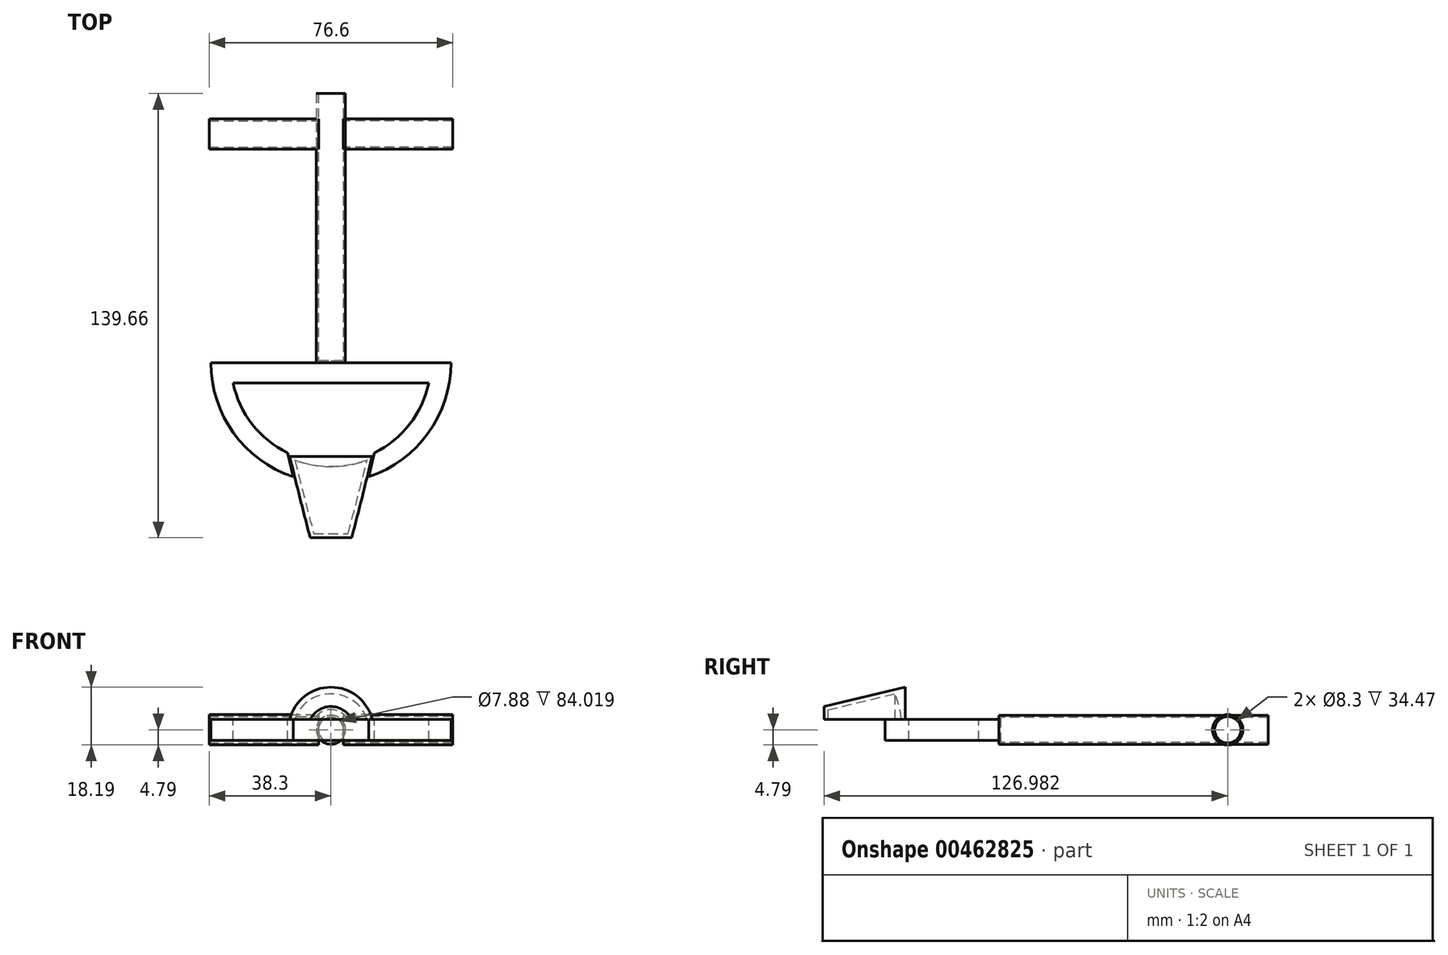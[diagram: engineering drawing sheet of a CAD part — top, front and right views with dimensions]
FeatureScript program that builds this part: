
annotation { "Feature Type Name" : "Feature", "Feature Type Description" : "" }
export const myFeature = defineFeature(function(context is Context, id is Id, definition is map)
    precondition{}
    {
        {
            var Q0;
            Q0=qCreatedBy(makeId("Top.planeOp"),FACE);
            var sketch = newSketch(context, id + "F0", { "sketchPlane" : qUnion([Q0])});
            skLineSegment(sketch, "E0.bottom", {"start": v(0, 0) * mm, "end": v(4.57, 0) * mm});
            skLineSegment(sketch, "E0.top", {"start": v(0, 84.65) * mm, "end": v(4.57, 84.65) * mm});
            skLineSegment(sketch, "E0.left", {"start": v(0, 0) * mm, "end": v(0, 84.65) * mm});
            skLineSegment(sketch, "E0.right", {"start": v(4.57, 0) * mm, "end": v(4.57, 84.65) * mm});
            skArc(sketch, "E1", {"start": v(-37.76, 0) * mm, "mid": v(0, -37.76) * mm, "end": v(37.76, 0) * mm});
            skLineSegment(sketch, "E2", {"start": v(-37.76, 0) * mm, "end": v(0, 0) * mm});
            skLineSegment(sketch, "E3", {"start": v(37.76, 0) * mm, "end": v(0, 0) * mm});
            skLineSegment(sketch, "E4", {"start": v(0, -29.44) * mm, "end": v(13.4, -29.44) * mm});
            skLineSegment(sketch, "E5", {"start": v(13.4, -29.44) * mm, "end": v(7.3, -55.01) * mm});
            skLineSegment(sketch, "E6", {"start": v(7.3, -55.01) * mm, "end": v(0, -55.01) * mm});
            skLineSegment(sketch, "E7", {"start": v(0, -55.01) * mm, "end": v(0, -29.44) * mm});
            skLineSegment(sketch, "E8", {"start": v(0, 0) * mm, "end": v(0, -37.76) * mm});
            skSolve(sketch);
        }
        {
            var Q0;
            Q0=makeQuery(id+"F0.imprint","IMPRINT",FACE,{"disambiguationData":[TD([[makeQuery(id+"F0.imprint","IMPRINT",EDGE,{"derivedFrom":sQuery(id+"F0.wireOp",EDGE,"E0.top")}),-1.0]])]});
            var Q1;
            {var subQ4=sQuery(id+"F0.wireOp",EDGE,"E6");Q1=makeQuery(id+"F0.imprint","IMPRINT",FACE,{"disambiguationData":[TD([[makeQuery(id+"F0.imprint","IMPRINT",EDGE,{"derivedFrom":subQ4}),-1.0]])]});}
            var Q2;
            {var subQ5=sQuery(id+"F0.wireOp",EDGE,"E4");Q2=makeQuery(id+"F0.imprint","IMPRINT",FACE,{"disambiguationData":[TD([[makeQuery(id+"F0.imprint","IMPRINT",EDGE,{"derivedFrom":subQ5}),-1.0]])]});}
            var Q3;
            Q3=sQuery(id+"F0.wireOp",EDGE,"E0.left");
            revolve(context, id + "F1", {"entities" : qUnion([Q0, Q1, Q2]), "axis" : qUnion([Q3]), "revolveType" : RevolveType.FULL});
        }
        {
            var Q0;
            {var subQ0=sQuery(id+"F0.wireOp",EDGE,"E4");Q0=makeQuery(id+"F0.imprint","IMPRINT",FACE,{"disambiguationData":[TD([[makeQuery(id+"F0.imprint","IMPRINT",EDGE,{"derivedFrom":subQ0}),1.0]])]});}
            var Q1;
            {var subQ0=sQuery(id+"F0.wireOp",EDGE,"E2");Q1=makeQuery(id+"F0.imprint","IMPRINT",FACE,{"disambiguationData":[TD([[makeQuery(id+"F0.imprint","IMPRINT",EDGE,{"derivedFrom":subQ0}),-1.0]])]});}
            var Q2;
            {var subQ5=sQuery(id+"F0.wireOp",EDGE,"E4");Q2=makeQuery(id+"F0.imprint","IMPRINT",FACE,{"disambiguationData":[TD([[makeQuery(id+"F0.imprint","IMPRINT",EDGE,{"derivedFrom":subQ5}),-1.0]])]});}
            extrude(context, id + "F2", {"entities" : qUnion([Q0, Q1, Q2]), "depth" : 6.6 * mm, "symmetric" : true});
        }
        {
            var Q0;
            Q0=qCreatedBy(makeId("Top.planeOp"),FACE);
            var sketch = newSketch(context, id + "F3", { "sketchPlane" : qUnion([Q0])});
            skLineSegment(sketch, "E9.bottom", {"start": v(3.83, 71.97) * mm, "end": v(38.3, 71.97) * mm});
            skLineSegment(sketch, "E9.top", {"start": v(3.83, 67.18) * mm, "end": v(38.3, 67.18) * mm});
            skLineSegment(sketch, "E9.left", {"start": v(3.83, 71.97) * mm, "end": v(3.83, 67.18) * mm});
            skLineSegment(sketch, "E9.right", {"start": v(38.3, 71.97) * mm, "end": v(38.3, 67.18) * mm});
            skSolve(sketch);
        }
        {
            var Q0;
            Q0 = qSketchRegion(id + "F3", true);
            var Q1;
            Q1=sQuery(id+"F3.wireOp",EDGE,"E9.bottom");
            revolve(context, id + "F4", {"entities" : qUnion([Q0]), "axis" : qUnion([Q1]), "revolveType" : RevolveType.FULL});
        }
        {
            var Q0;
            Q0=makeQuery(id+"F4.opRevolve","SWEPT_BODY",BODY,{"disambiguationData":[OSD([sQuery(id+"F3.wireOp",EDGE,"E9.bottom"),sQuery(id+"F3.wireOp",EDGE,"E9.top"),sQuery(id+"F3.wireOp",EDGE,"E9.left"),sQuery(id+"F3.wireOp",EDGE,"E9.right")])]});
            var Q1;
            Q1=qCreatedBy(makeId("Right.planeOp"),FACE);
            mirror(context, id + "F5", {"entities" : qUnion([Q0]), "mirrorPlane" : qUnion([Q1])});
        }
        {
            var Q0;
            Q0=makeQuery(id+"F2.opExtrude","CAP_FACE",FACE,{"disambiguationData":[OSD([sQuery(id+"F0.wireOp",EDGE,"E1"),sQuery(id+"F0.wireOp",EDGE,"E2"),sQuery(id+"F0.wireOp",EDGE,"E3")])],"isStart":false});
            var sketch = newSketch(context, id + "F6", { "sketchPlane" : qUnion([Q0])});
            skLineSegment(sketch, "E10.0", {"start": v(37.76, 0) * mm, "end": v(0, 0) * mm});
            skLineSegment(sketch, "E10.1", {"start": v(-37.76, 0) * mm, "end": v(0, 0) * mm});
            skArc(sketch, "E10.2", {"start": v(-37.76, 0) * mm, "mid": v(0, -37.76) * mm, "end": v(37.76, 0) * mm});
            skLineSegment(sketch, "E11.0", {"start": v(30.76, -6.35) * mm, "end": v(0, -6.35) * mm});
            skArc(sketch, "E11.1", {"start": v(-30.76, -6.35) * mm, "mid": v(0, -31.4) * mm, "end": v(30.76, -6.35) * mm});
            skLineSegment(sketch, "E11.2", {"start": v(-30.76, -6.35) * mm, "end": v(0, -6.35) * mm});
            skSolve(sketch);
        }
        {
            var Q0;
            Q0=makeQuery(id+"F6.imprint","IMPRINT",FACE,{"disambiguationData":[TD([[makeQuery(id+"F6.imprint","IMPRINT",EDGE,{"derivedFrom":sQuery(id+"F6.wireOp",EDGE,"E11.0")}),1.0]])]});
            var Q1;
            Q1 = qConstructionFilter(qBodyType(qCreatedBy(id + "F6" ,EDGE), BodyType.WIRE), ConstructionObject.NO);
            extrude(context, id + "F7", {"entities" : qUnion([Q0]), "operationType" : NewBodyOperationType.REMOVE, "surfaceEntities" : qUnion([Q1]), "oppositeDirection" : true, "depth" : 25.4 * mm});
        }
        {
            var Q0;
            Q0=makeQuery(id+"F1.opRevolve","SWEPT_FACE",FACE,{"disambiguationData":[OSD([sQuery(id+"F0.wireOp",EDGE,"E4")])]});
            shell(context, id + "F8", {"entities" : qUnion([Q0]), "thickness" : 1.27 * mm});
        }
        {
            var Q0;
            Q0=makeQuery(id+"F2.opExtrude","CAP_FACE",FACE,{"disambiguationData":[OSD([sQuery(id+"F0.wireOp",EDGE,"E1"),sQuery(id+"F0.wireOp",EDGE,"E2"),sQuery(id+"F0.wireOp",EDGE,"E3")])],"isStart":false});
            var sketch = newSketch(context, id + "F9", { "sketchPlane" : qUnion([Q0])});
            skLineSegment(sketch, "E12.0", {"start": v(13.4, -29.44) * mm, "end": v(7.3, -55.01) * mm});
            skLineSegment(sketch, "E13.MirrorCS", {"start": v(-13.4, -29.44) * mm, "end": v(-7.3, -55.01) * mm});
            skLineSegment(sketch, "E14", {"start": v(-13.4, -29.44) * mm, "end": v(-16.33, -17.12) * mm});
            skLineSegment(sketch, "E15", {"start": v(-16.33, -17.12) * mm, "end": v(16.33, -17.12) * mm});
            skLineSegment(sketch, "E16", {"start": v(16.33, -17.12) * mm, "end": v(13.4, -29.44) * mm});
            skLineSegment(sketch, "E17", {"start": v(-7.3, -55.01) * mm, "end": v(7.3, -55.01) * mm});
            skSolve(sketch);
        }
        {
            var Q0;
            Q0 = qSketchRegion(id + "F9", true);
            extrude(context, id + "F10", {"entities" : qUnion([Q0]), "operationType" : NewBodyOperationType.REMOVE, "oppositeDirection" : true, "depth" : 25.4 * mm});
        }
        {
            var Q0;
            Q0=makeQuery(id+"F1.opRevolve","SWEPT_FACE",FACE,{"disambiguationData":[OSD([sQuery(id+"F0.wireOp",EDGE,"E0.top")])]});
            var Q1;
            Q1=makeQuery(id+"F1.opRevolve","SWEPT_FACE",FACE,{"disambiguationData":[OSD([sQuery(id+"F0.wireOp",EDGE,"E3")])]});
            var Q2;
            Q2=makeQuery(id+"F4.opRevolve","SWEPT_FACE",FACE,{"disambiguationData":[OSD([sQuery(id+"F3.wireOp",EDGE,"E9.right")])]});
            var Q3;
            Q3=makeQuery(id+"F5.opPattern","COPY",FACE,{"derivedFrom":makeQuery(id+"F4.opRevolve","SWEPT_FACE",FACE,{"disambiguationData":[OSD([sQuery(id+"F3.wireOp",EDGE,"E9.left")])]}),"instanceName":"1"});
            var Q4;
            Q4=makeQuery(id+"F4.opRevolve","SWEPT_FACE",FACE,{"disambiguationData":[OSD([sQuery(id+"F3.wireOp",EDGE,"E9.left")])]});
            var Q5;
            Q5=makeQuery(id+"F5.opPattern","COPY",FACE,{"derivedFrom":makeQuery(id+"F4.opRevolve","SWEPT_FACE",FACE,{"disambiguationData":[OSD([sQuery(id+"F3.wireOp",EDGE,"E9.right")])]}),"instanceName":"1"});
            shell(context, id + "F11", {"entities" : qUnion([Q0, Q1, Q2, Q3, Q4, Q5]), "thickness" : 0.64 * mm});
        }
    });
